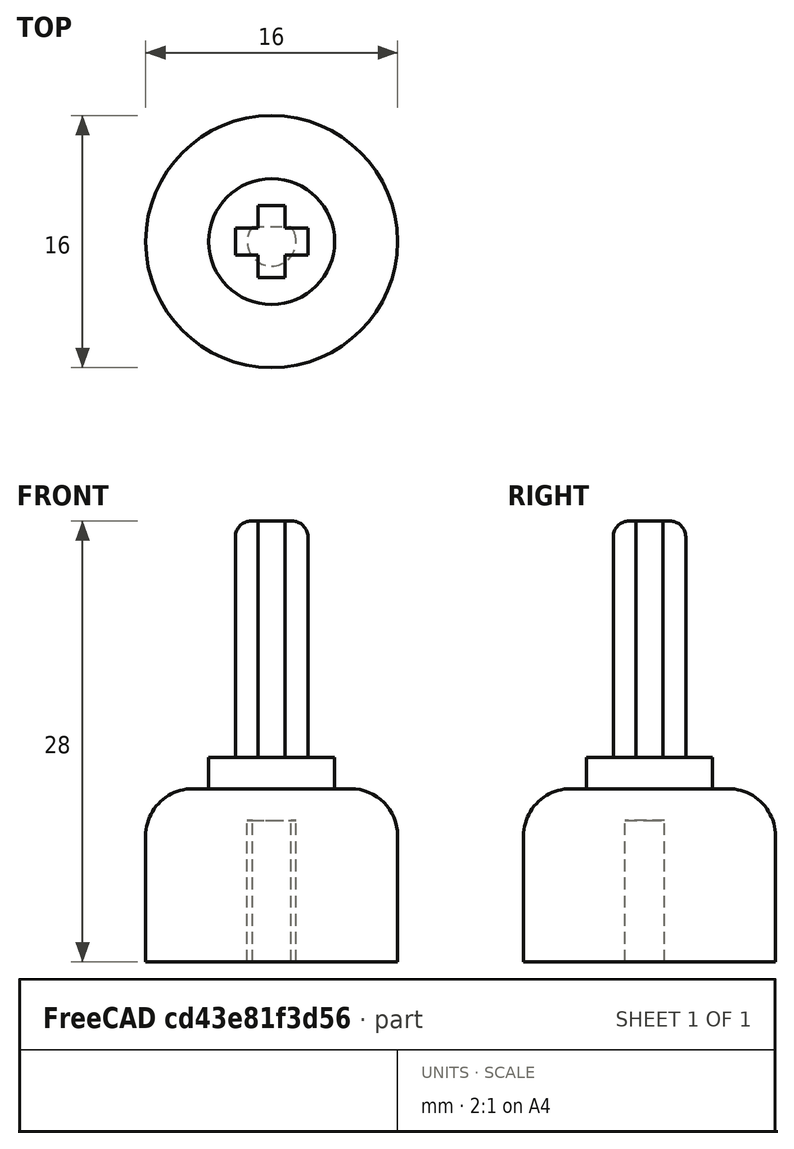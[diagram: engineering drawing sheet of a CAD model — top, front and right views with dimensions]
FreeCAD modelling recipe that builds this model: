
FCSTD DOCUMENT  (FreeCAD 0.18R16131 (Git))
Label: EjeTransmisionMinimotor
License: All rights reserved
LicenseURL: http://en.wikipedia.org/wiki/All_rights_reserved
objects: Part::Cylinder×3, Part::Box×3, Part::Fillet×3, Part::MultiFuse×2, Part::MultiCommon×1, Part::Cut×1
note: 13 computed .brp shape members not serialized (recipe doc carries the construction recipe); baked Part::Feature solids carry a one-line shape summary decoded from their .brp

FEATURE [Part::Cylinder] Cylinder  label="Cilindro"
  Angle = 360
  AttacherType = Attacher::AttachEngine3D
  Height = 11
  Radius = 8
FEATURE [Part::Cylinder] Cylinder001  label="Cilindro001"
  Angle = 360
  AttacherType = Attacher::AttachEngine3D
  Height = 9
  Radius = 1.55
FEATURE [Part::Box] Box  label="Cubo"
  AttacherType = Attacher::AttachEngine3D
  Height = 11
  Length = 10
  Placement = pos=(-5,-1.55,0) rot=(0,0,1;0rad)
  Width = 2.5
FEATURE [Part::MultiCommon] Common  label="Taladro"
  Shapes = -> [Box,Cylinder001]
FEATURE [Part::Cylinder] Cylinder002  label="Cilindro002"
  Angle = 360
  AttacherType = Attacher::AttachEngine3D
  Height = 2
  Placement = pos=(0,0,11) rot=(0,0,1;0rad)
  Radius = 4
FEATURE [Part::Box] Box001  label="Cubo001"
  AttacherType = Attacher::AttachEngine3D
  Height = 15
  Length = 1.7
  Placement = pos=(-0.85,-2.3,22) rot=(0,0,1;0rad)
  Width = 4.6
FEATURE [Part::Box] Box002  label="Cubo002"
  AttacherType = Attacher::AttachEngine3D
  Height = 15
  Length = 4.6
  Placement = pos=(-2.3,-0.85,22) rot=(0,0,1;0rad)
  Width = 1.7
FEATURE [Part::Fillet] Fillet
  Base = -> Box001
  Edges = 2 edges r=1: [Edge10,Edge12]
FEATURE [Part::Fillet] Fillet001
  Base = -> Box002
  Edges = 2 edges r=1: [Edge2,Edge6]
FEATURE [Part::Cut] Cut
  Base = -> Cylinder
  Tool = -> Common
FEATURE [Part::MultiFuse] Fusion
  Placement = pos=(0,0,-9) rot=(0,0,1;0rad)
  Shapes = -> [Fillet,Fillet001]
FEATURE [Part::Fillet] Fillet002
  Base = -> Cut
  Edges = 1 edges r=3: [Edge1]
FEATURE [Part::MultiFuse] Fusion001  label="Eje rueda motor"
  Shapes = -> [Fusion,Cylinder002,Fillet002]
